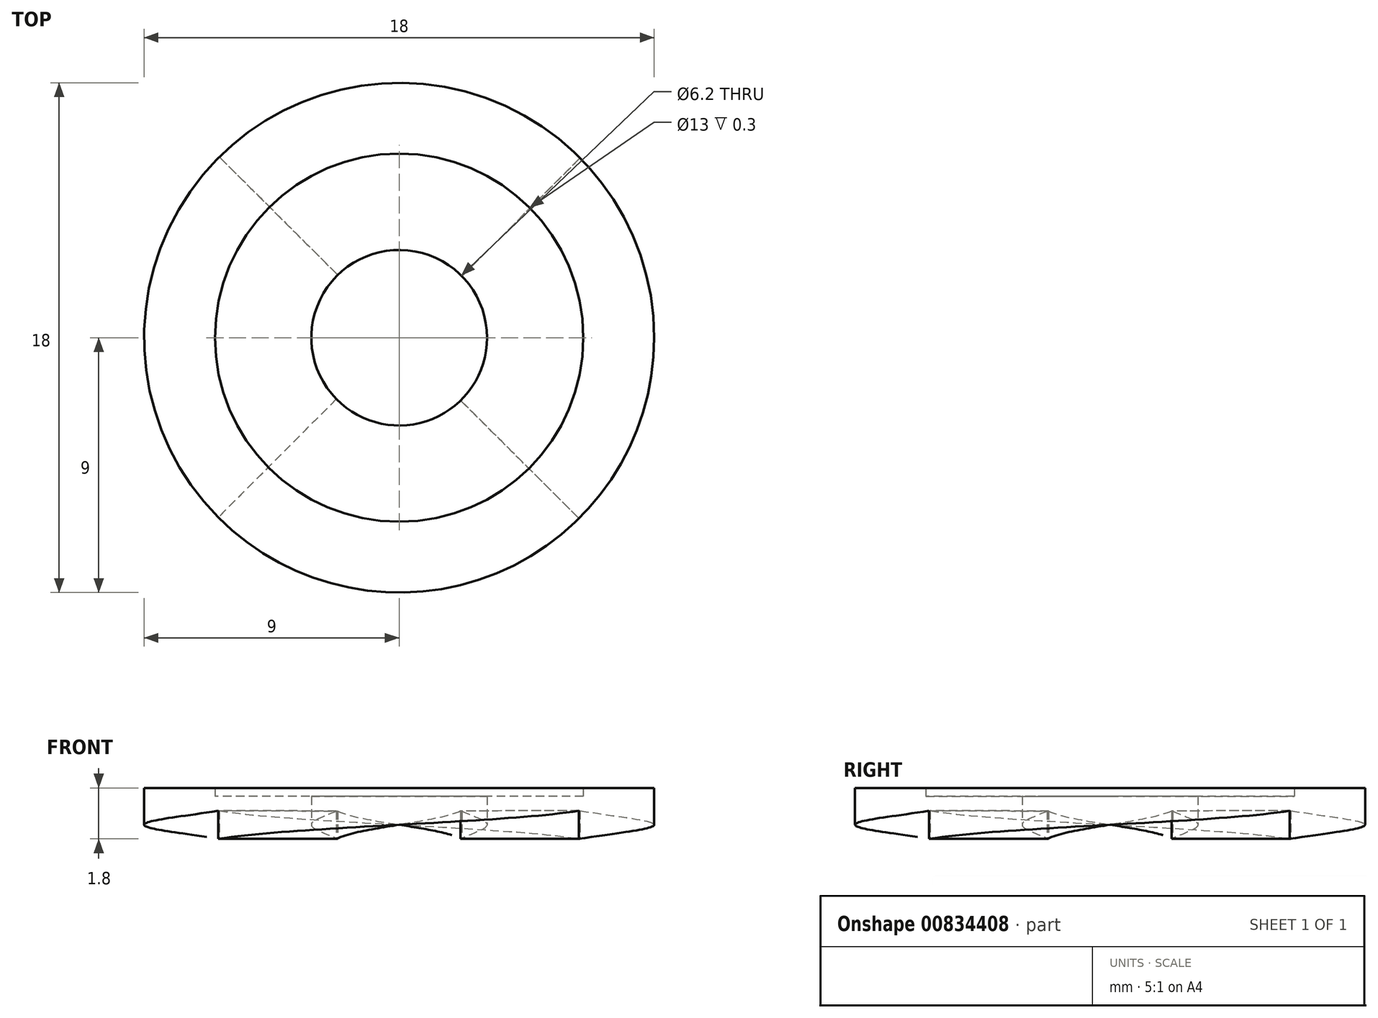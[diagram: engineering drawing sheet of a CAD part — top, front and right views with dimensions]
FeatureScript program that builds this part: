
annotation { "Feature Type Name" : "Feature", "Feature Type Description" : "" }
export const myFeature = defineFeature(function(context is Context, id is Id, definition is map)
    precondition{}
    {
        {
            var Q0;
            Q0=qCreatedBy(makeId("Front.planeOp"),FACE);
            var sketch = newSketch(context, id + "F0", { "sketchPlane" : qUnion([Q0])});
            skLineSegment(sketch, "E0", {"start": v(-0.05, 0) * mm, "end": v(0.05, 1) * mm});
            skLineSegment(sketch, "E1", {"start": v(0.05, 1) * mm, "end": v(0.05, 1.5) * mm});
            skLineSegment(sketch, "E2", {"start": v(0.05, 1.5) * mm, "end": v(-0.05, 1.5) * mm});
            skLineSegment(sketch, "E3", {"start": v(-0.05, 1.5) * mm, "end": v(-0.05, 0) * mm});
            skLineSegment(sketch, "E4", {"start": v(0, 13.58) * mm, "end": v(0, 25.88) * mm});
            skSolve(sketch);
        }
        {
            var Q0;
            Q0=qCreatedBy(makeId("Front.planeOp"),FACE);
            cPlane(context, id + "F1", {"entities" : qUnion([Q0]), "cplaneType" : CPlaneType.OFFSET, "offset" : 20 * mm, "width" : 150 * mm, "height" : 150 * mm});
        }
        {
            var Q0;
            Q0=qCreatedBy(id+"F1.planeOp",FACE);
            var sketch = newSketch(context, id + "F2", { "sketchPlane" : qUnion([Q0])});
            skLineSegment(sketch, "E5", {"start": v(-20, 0) * mm, "end": v(20, 1) * mm});
            skLineSegment(sketch, "E6", {"start": v(20, 1) * mm, "end": v(20, 1.5) * mm});
            skLineSegment(sketch, "E7", {"start": v(20, 1.5) * mm, "end": v(-20, 1.5) * mm});
            skLineSegment(sketch, "E8", {"start": v(-20, 1.5) * mm, "end": v(-20, 0) * mm});
            skSolve(sketch);
        }
        {
            var Q0;
            Q0=makeQuery(id+"F0.imprint","IMPRINT",FACE,{"disambiguationData":[TD([[makeQuery(id+"F0.imprint","IMPRINT",EDGE,{"derivedFrom":sQuery(id+"F0.wireOp",EDGE,"E0")}),1.0]])]});
            var Q1;
            Q1=makeQuery(id+"F2.imprint","IMPRINT",FACE,{"disambiguationData":[TD([[makeQuery(id+"F2.imprint","IMPRINT",EDGE,{"derivedFrom":sQuery(id+"F2.wireOp",EDGE,"E5")}),1.0]])]});
            loft(context, id + "F3", {"sheetProfilesArray" : [{ "sheetProfileEntities" : qUnion([Q0]) }, { "sheetProfileEntities" : qUnion([Q1]) }]});
        }
        {
            var Q0;
            Q0=makeQuery(id+"F3.opLoft","SWEPT_BODY",BODY,{"disambiguationData":[OSD([makeQuery(id+"F0.imprint","IMPRINT",FACE,{"disambiguationData":[TD([[makeQuery(id+"F0.imprint","IMPRINT",EDGE,{"derivedFrom":sQuery(id+"F0.wireOp",EDGE,"E0")}),1.0]])]}),makeQuery(id+"F2.imprint","IMPRINT",FACE,{"disambiguationData":[TD([[makeQuery(id+"F2.imprint","IMPRINT",EDGE,{"derivedFrom":sQuery(id+"F2.wireOp",EDGE,"E5")}),1.0]])]})])]});
            var Q1;
            Q1=sQuery(id+"F0.wireOp",EDGE,"E4");
            circularPattern(context, id + "F4", {"operationType" : NewBodyOperationType.ADD, "entities" : qUnion([Q0]), "axis" : qUnion([Q1]), "angle" : 360 * degree, "instanceCount" : 4, "equalSpace" : true});
        }
        {
            var Q0;
            Q0=qCreatedBy(makeId("Top.planeOp"),FACE);
            var sketch = newSketch(context, id + "F5", { "sketchPlane" : qUnion([Q0])});
            skCircle(sketch, "E9", {"center": v(0, 0) * mm, "radius": 9 * mm});
            skLineSegment(sketch, "E10.bottom", {"start": v(2.02, 3.02) * mm, "end": v(-2.02, 3.02) * mm});
            skLineSegment(sketch, "E10.top", {"start": v(2.02, -3.02) * mm, "end": v(-2.02, -3.02) * mm});
            skLineSegment(sketch, "E10.left", {"start": v(2.02, 3.02) * mm, "end": v(2.02, -3.02) * mm});
            skLineSegment(sketch, "E10.right", {"start": v(-2.02, 3.02) * mm, "end": v(-2.02, -3.02) * mm});
            skCircle(sketch, "E11", {"center": v(0, 0) * mm, "radius": 3.1 * mm});
            skCircle(sketch, "E12", {"center": v(0, 0) * mm, "radius": 2.02 * mm, "construction": true});
            skCircle(sketch, "E13", {"center": v(0, 0) * mm, "radius": 5 * mm});
            skCircle(sketch, "E14", {"center": v(0, 0) * mm, "radius": 6.5 * mm});
            skSolve(sketch);
        }
        {
            var Q0;
            Q0=makeQuery(id+"F5.imprint","IMPRINT",FACE,{"disambiguationData":[TD([[makeQuery(id+"F5.imprint","IMPRINT",EDGE,{"derivedFrom":sQuery(id+"F5.wireOp",EDGE,"E9")}),1.0]])]});
            var Q1;
            Q1=makeQuery(id+"F5.imprint","IMPRINT",FACE,{"disambiguationData":[TD([[makeQuery(id+"F5.imprint","IMPRINT",EDGE,{"derivedFrom":sQuery(id+"F5.wireOp",EDGE,"E13")}),1.0]])]});
            var Q2;
            {var subQ0=sQuery(id+"F5.wireOp",EDGE,"E10.right");var subQ1=sQuery(id+"F5.wireOp",EDGE,"E10.top");var subQ2=makeQuery(id+"F5.imprint","INTERSECT",VERTEX,{"derivedFrom":[subQ1,subQ0]});Q2=makeQuery(id+"F5.imprint","IMPRINT",FACE,{"disambiguationData":[TD([[makeQuery(id+"F5.imprint","IMPRINT",EDGE,{"disambiguationData":[TD([[subQ2,1.0]])],"derivedFrom":subQ1}),-1.0]])]});}
            var Q3;
            {var subQ0=sQuery(id+"F5.wireOp",EDGE,"E10.left");var subQ1=sQuery(id+"F5.wireOp",EDGE,"E10.top");var subQ2=makeQuery(id+"F5.imprint","INTERSECT",VERTEX,{"derivedFrom":[subQ1,subQ0]});Q3=makeQuery(id+"F5.imprint","IMPRINT",FACE,{"disambiguationData":[TD([[makeQuery(id+"F5.imprint","IMPRINT",EDGE,{"disambiguationData":[TD([[subQ2,-1.0]])],"derivedFrom":subQ1}),-1.0]])]});}
            var Q4;
            {var subQ0=sQuery(id+"F5.wireOp",EDGE,"E10.left");var subQ1=sQuery(id+"F5.wireOp",EDGE,"E10.bottom");var subQ2=makeQuery(id+"F5.imprint","INTERSECT",VERTEX,{"derivedFrom":[subQ1,subQ0]});Q4=makeQuery(id+"F5.imprint","IMPRINT",FACE,{"disambiguationData":[TD([[makeQuery(id+"F5.imprint","IMPRINT",EDGE,{"disambiguationData":[TD([[subQ2,-1.0]])],"derivedFrom":subQ1}),1.0]])]});}
            var Q5;
            {var subQ0=sQuery(id+"F5.wireOp",EDGE,"E10.right");var subQ1=sQuery(id+"F5.wireOp",EDGE,"E10.bottom");var subQ2=makeQuery(id+"F5.imprint","INTERSECT",VERTEX,{"derivedFrom":[subQ1,subQ0]});Q5=makeQuery(id+"F5.imprint","IMPRINT",FACE,{"disambiguationData":[TD([[makeQuery(id+"F5.imprint","IMPRINT",EDGE,{"disambiguationData":[TD([[subQ2,1.0]])],"derivedFrom":subQ1}),1.0]])]});}
            var Q6;
            Q6=makeQuery(id+"F5.imprint","IMPRINT",FACE,{"disambiguationData":[TD([[makeQuery(id+"F5.imprint","IMPRINT",EDGE,{"derivedFrom":sQuery(id+"F5.wireOp",EDGE,"E13")}),-1.0]])]});
            extrude(context, id + "F6", {"entities" : qUnion([Q0, Q1, Q2, Q3, Q4, Q5, Q6]), "depth" : 10 * mm, "offsetDistance" : 25 * mm});
        }
        {
            var Q0;
            Q0=makeQuery(id+"F6.opExtrude","SWEPT_BODY",BODY,{"disambiguationData":[OSD([sQuery(id+"F5.wireOp",EDGE,"E9"),sQuery(id+"F5.wireOp",EDGE,"E10.bottom"),sQuery(id+"F5.wireOp",EDGE,"E10.top"),sQuery(id+"F5.wireOp",EDGE,"E10.left"),sQuery(id+"F5.wireOp",EDGE,"E10.right")])]});
            var Q1;
            Q1=makeQuery(id+"F3.opLoft","SWEPT_BODY",BODY,{"disambiguationData":[OSD([makeQuery(id+"F0.imprint","IMPRINT",FACE,{"disambiguationData":[TD([[makeQuery(id+"F0.imprint","IMPRINT",EDGE,{"derivedFrom":sQuery(id+"F0.wireOp",EDGE,"E0")}),1.0]])]}),makeQuery(id+"F2.imprint","IMPRINT",FACE,{"disambiguationData":[TD([[makeQuery(id+"F2.imprint","IMPRINT",EDGE,{"derivedFrom":sQuery(id+"F2.wireOp",EDGE,"E5")}),1.0]])]})])]});
            booleanBodies(context, id + "F7", {"operationType" : BooleanOperationType.INTERSECTION, "tools" : qUnion([Q0, Q1])});
        }
        {
            var Q0;
            Q0=makeQuery(id+"F5.imprint","IMPRINT",FACE,{"disambiguationData":[TD([[makeQuery(id+"F5.imprint","IMPRINT",EDGE,{"derivedFrom":sQuery(id+"F5.wireOp",EDGE,"E9")}),1.0]])]});
            extrude(context, id + "F8", {"entities" : qUnion([Q0]), "operationType" : NewBodyOperationType.ADD, "depth" : 1.8 * mm, "offsetDistance" : 25 * mm, "hasSecondDirection" : true, "secondDirectionOppositeDirection" : false, "secondDirectionDepth" : 1.5 * mm});
        }
    });
